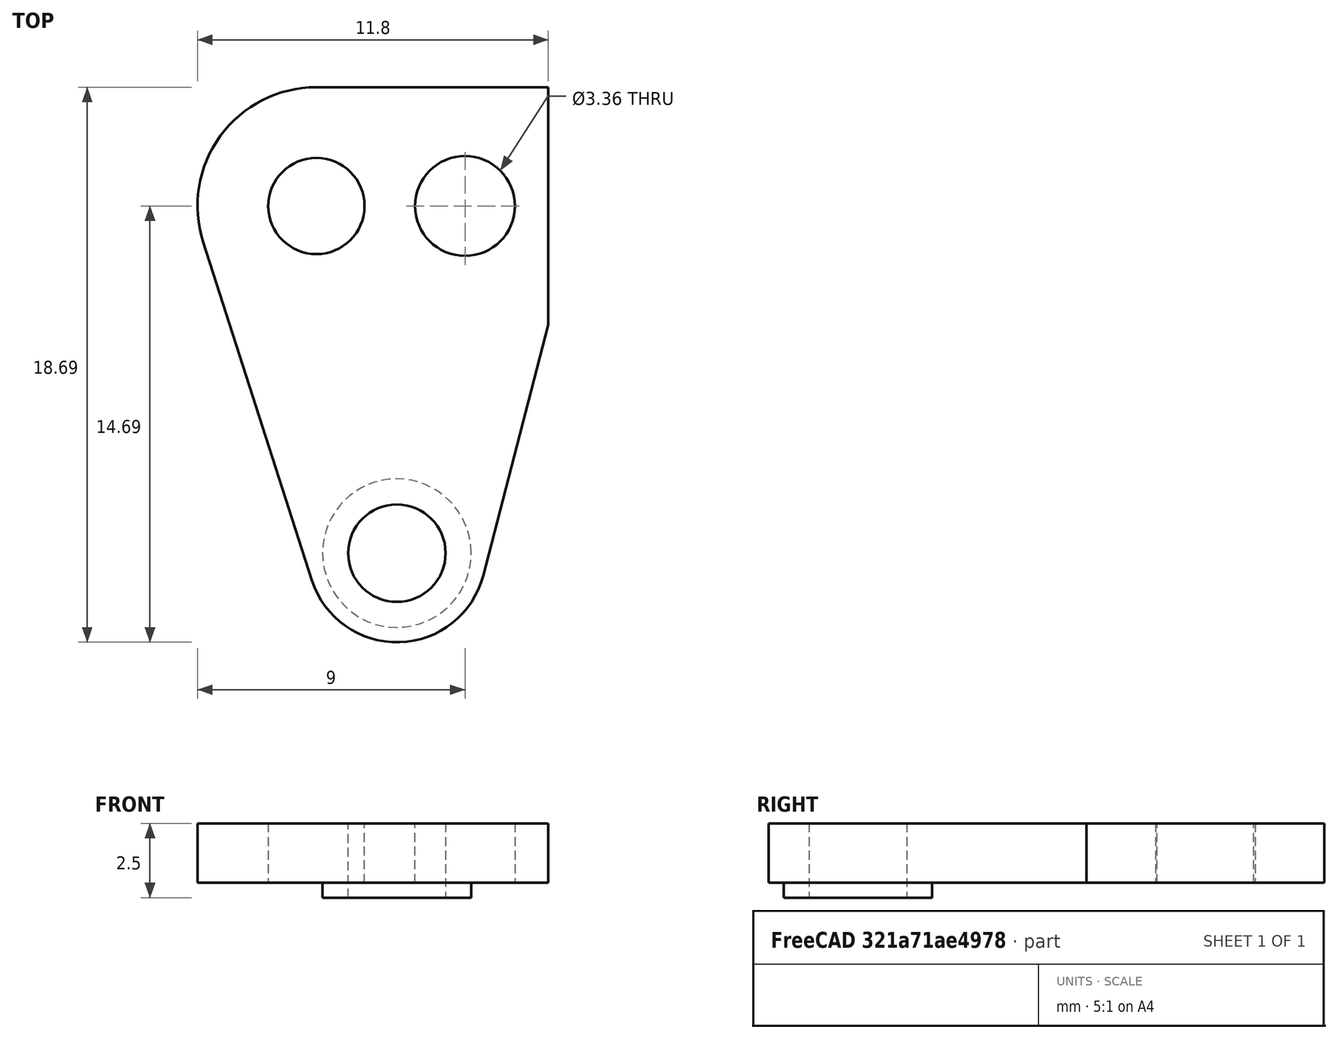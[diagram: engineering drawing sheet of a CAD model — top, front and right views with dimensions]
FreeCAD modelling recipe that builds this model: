
FCSTD DOCUMENT  (FreeCAD 1.0R39285 (Git))
Label: WheelLinkageTopRight
License: All rights reserved
LicenseURL: https://en.wikipedia.org/wiki/All_rights_reserved
objects: PartDesign::SubShapeBinder×1, Part::Mirroring×1, App::Part×1
note: 2 computed .brp shape members not serialized (recipe doc carries the construction recipe); baked Part::Feature solids carry a one-line shape summary decoded from their .brp
EXTERNAL_REF file=WheelLinkageTopLeft.FCStd obj=Part

FEATURE [PartDesign::SubShapeBinder] Binder  label="WheelLinkageTopLeftBody"
  BindCopyOnChange = 0
  BindMode = 0
  ClaimChildren = false
  Context = -> Part [Binder.]
  Fuse = false
  MakeFace = true
  OffsetFill = false
  OffsetIntersection = false
  OffsetJoinType = 0
  OffsetOpenResult = false
  PartialLoad = false
  Refine = true
  Relative = true
  Support = -> [<external WheelLinkageTopLeft.FCStd>#Part[Body.]]
  _Version = 2
FEATURE [Part::Mirroring] Part__Mirroring  label="WheelLinkageTopRightBody"
  Base = (0,0,0)
  Normal = (1,0,0)
  Source = -> Binder
FEATURE [App::Part] Part  label="WheelLinkageTopRightPart"
  Group = -> [Binder,Part__Mirroring]
  Origin = -> Origin
